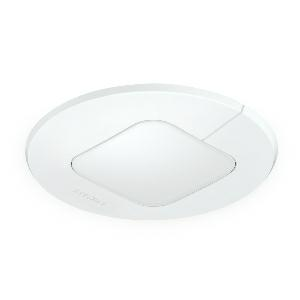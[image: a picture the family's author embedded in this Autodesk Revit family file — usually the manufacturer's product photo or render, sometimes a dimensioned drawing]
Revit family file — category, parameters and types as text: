
# Revit family: ir_quattro_slim_xs_057527
name_source: partatom
category: Elektroinstallationen
revit_build: Autodesk Revit 2016 (Build: 20190508_0715(x64)
units: mm (PartAtom-declared; Revit-internal decimal feet)

## family parameters
Basisbauteil = Fläche
Beim Laden mit Abzugskörper schneiden = Nein
Bemaßung runder Anschluss = Durchmesser verwenden
Beschriftungsausrichtung beibehalten = Nein
Gemeinsam genutzt = Nein
Raumberechnungspunkt = Nein
Teiletyp = Normal

## types (1)
- IR Quattro SLIM XS
    Apparent Load = 0 VA
    Beschreibung = Type: Presence detector; Dimensions (Ø x H): 94 x 55 mm; Mains power supply: 16 V; Sensor Technology: passive infrared; Application, place: Indoors; Application, room: one-person office, hotel room, care room, function room / ancillary room, WC / washroom, Indoors; Installation site: ceiling; Installation: Concealed wiring; Switching zones: 408 switching zones; Electronic scalability: No; Mechanical scalability: No; Mounting height: 2,50 – 4,00 m; Optimum mounting height: 2,8 m; Detection angle: 360 °; Sneak-by guard: No; Capability of masking out individual segments: No; Reach, detail: Retina lens and hexagonal Fresnel structure; Reach, radial: 4 x 4 m (16 m²); Reach, tangential: 4 x 4 m (16 m²); Reach, presence: 4 x 4 m (16 m²); Twilight setting TEACH: Yes; Twilight setting: 10 – 1000 lx; Time setting: 30 sec – 30 min; Switching output 2, floating: No; Control output, Dali: Addressable/slave; Constant-lighting control: Yes; Basic light level function: No; Settings via: Bus; With remote control: No; Interconnection: Yes; IP-rating: IP20; Material: Plastic; Ambient temperature: 0 – 40 °C; Colour: white; Colour, RAL: 9010; Manufacturer's Warranty: 5 years; Version: DALI-2 Input Device - round; PU1, EAN: 4007841057527
    Height = 0 mm  [stored 0 ft]
    Hersteller = Steinel
    Length = 94 mm  [stored 0.308399 ft]
    Maximum range = 2.654 m
    ModVariant = Nein
    Modell = 057527
    Mounting Place = Ceiling
    Mounting Type = Recessed
    Number of Poles = 1
    OnlyDefault = Ja
    Power Factor = 1
    Product Name = IR Quattro SLIM XS
    Product group = Presence detector
    ProductGroupID = 4
    Protection Class = Protection class
    Protection Degree = IP 20
    RlxData = <blob elided: 157213 chars, md5=fcb4d4fe>
    Sensor characteristics = Circular 300°-360°
    Sensor type = Passive (infrared)
    SensorDataFile = <blob elided: 166498 chars, md5=02ce23fe>
    Type of entry = Presence, Motion
    Typenbild = produkt1_057527.jpg
    Typenkommentare = Product without accessories
    URL = http://relux.com
    VarID = ---
    Voltage = 0 V
    Vorgabe-Ansicht = 1800 mm
    Weight = 0.00 kg
    Width = 0 mm  [stored 0 ft]

note: [stored X ft] marks values corroborated as IEEE doubles in the binary element streams (Revit-internal decimal feet)

## geometry (parser evidence)
native form markers: Blend x4, Sweep x15
no freeform markers — native parametric forms only
